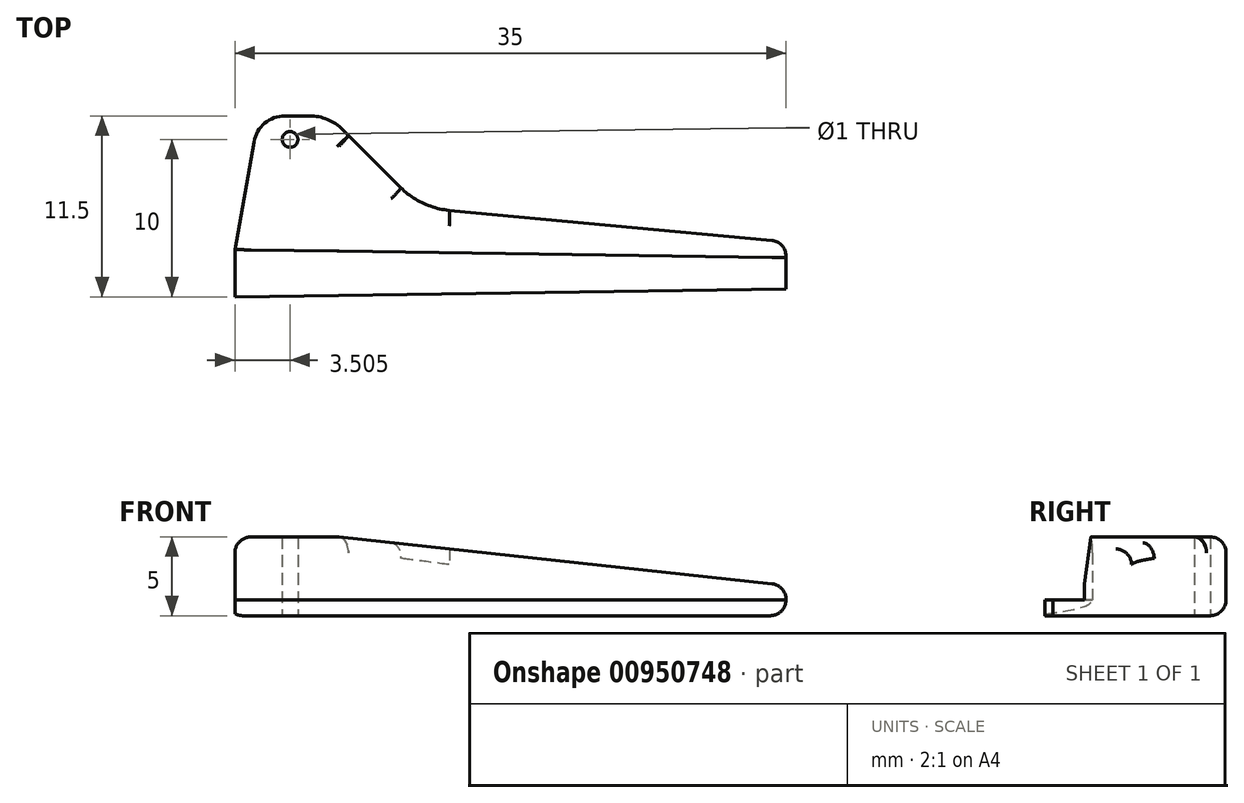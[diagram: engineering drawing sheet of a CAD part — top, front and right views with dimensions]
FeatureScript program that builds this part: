
annotation { "Feature Type Name" : "Feature", "Feature Type Description" : "" }
export const myFeature = defineFeature(function(context is Context, id is Id, definition is map)
    precondition{}
    {
        {
            var Q0;
            Q0=qCreatedBy(makeId("Top.planeOp"),FACE);
            var sketch = newSketch(context, id + "F0", { "sketchPlane" : qUnion([Q0])});
            skLineSegment(sketch, "E0", {"start": v(0.26, 1.5) * mm, "end": v(1.47, 8.35) * mm});
            skLineSegment(sketch, "E1", {"start": v(3.44, 10) * mm, "end": v(5, 10) * mm});
            skLineSegment(sketch, "E2", {"start": v(7.11, 9.12) * mm, "end": v(10.8, 5.44) * mm});
            skLineSegment(sketch, "E3", {"start": v(13.86, 4) * mm, "end": v(34.36, 2.08) * mm});
            skLineSegment(sketch, "E4", {"start": v(35.26, 1.09) * mm, "end": v(35.26, 0) * mm});
            skPoint(sketch, "E5.visualSharp", {"position": v(1.76, 10) * mm});
            skArc(sketch, "E5.filletArc", {"start": v(3.44, 10) * mm, "mid": v(2.16, 9.53) * mm, "end": v(1.47, 8.35) * mm});
            skPoint(sketch, "E6.visualSharp", {"position": v(6.23, 10) * mm});
            skArc(sketch, "E6.filletArc", {"start": v(7.11, 9.12) * mm, "mid": v(6.14, 9.77) * mm, "end": v(5, 10) * mm});
            skLineSegment(sketch, "E7", {"start": v(0.26, 1.5) * mm, "end": v(35.26, 1) * mm});
            skLineSegment(sketch, "E8", {"start": v(0.26, 1.5) * mm, "end": v(0.26, 0) * mm});
            skPoint(sketch, "E9.orphan", {"position": v(0, 0) * mm});
            skPoint(sketch, "E10.visualSharp", {"position": v(12.07, 4.17) * mm});
            skArc(sketch, "E10.filletArc", {"start": v(10.8, 5.44) * mm, "mid": v(12.2, 4.45) * mm, "end": v(13.86, 4) * mm});
            skLineSegment(sketch, "E11", {"start": v(1.23, 7) * mm, "end": v(9.23, 7) * mm, "construction": true});
            skCircle(sketch, "E12", {"center": v(3.76, 8.5) * mm, "radius": 0.5 * mm});
            skPoint(sketch, "E13.visualSharp", {"position": v(35.26, 2) * mm});
            skArc(sketch, "E13.filletArc", {"start": v(35.26, 1.09) * mm, "mid": v(35, 1.76) * mm, "end": v(34.36, 2.08) * mm});
            skArc(sketch, "E14.MirrorCS", {"start": v(35.26, -1.09) * mm, "mid": v(35, -1.76) * mm, "end": v(34.36, -2.08) * mm});
            skPoint(sketch, "E15.MirrorP", {"position": v(1.76, -10) * mm});
            skArc(sketch, "E16.MirrorCS", {"start": v(7.11, -9.12) * mm, "mid": v(6.14, -9.77) * mm, "end": v(5, -10) * mm});
            skArc(sketch, "E17.MirrorCS", {"start": v(10.8, -5.44) * mm, "mid": v(12.2, -4.45) * mm, "end": v(13.86, -4) * mm});
            skLineSegment(sketch, "E18.MirrorCS", {"start": v(3.44, -10) * mm, "end": v(5, -10) * mm});
            skPoint(sketch, "E19.MirrorP", {"position": v(35.26, -2) * mm});
            skCircle(sketch, "E20.MirrorC", {"center": v(3.76, -8.5) * mm, "radius": 0.5 * mm});
            skLineSegment(sketch, "E21.MirrorCS", {"start": v(7.11, -9.12) * mm, "end": v(10.8, -5.44) * mm});
            skLineSegment(sketch, "E22.MirrorCS", {"start": v(0.26, -1.5) * mm, "end": v(35.26, -1) * mm});
            skLineSegment(sketch, "E23.MirrorCS", {"start": v(1.23, -7) * mm, "end": v(9.23, -7) * mm, "construction": true});
            skPoint(sketch, "E24.MirrorP", {"position": v(6.23, -10) * mm});
            skArc(sketch, "E25.MirrorCS", {"start": v(3.44, -10) * mm, "mid": v(2.16, -9.53) * mm, "end": v(1.47, -8.35) * mm});
            skPoint(sketch, "E26.MirrorP", {"position": v(12.07, -4.17) * mm});
            skLineSegment(sketch, "E27.MirrorCS", {"start": v(0.26, -1.5) * mm, "end": v(1.47, -8.35) * mm});
            skLineSegment(sketch, "E28.MirrorCS", {"start": v(13.86, -4) * mm, "end": v(34.36, -2.08) * mm});
            skLineSegment(sketch, "E29.MirrorCS", {"start": v(0.26, -1.5) * mm, "end": v(0.26, 0) * mm});
            skLineSegment(sketch, "E30.MirrorCS", {"start": v(35.26, -1.09) * mm, "end": v(35.26, 0) * mm});
            skSolve(sketch);
        }
        {
            var Q0;
            Q0=makeQuery(id+"F0.imprint","IMPRINT",FACE,{"disambiguationData":[TD([[makeQuery(id+"F0.imprint","IMPRINT",EDGE,{"derivedFrom":sQuery(id+"F0.wireOp",EDGE,"E0")}),-1.0]])]});
            var Q1;
            {var subQ1=sQuery(id+"F0.wireOp",EDGE,"E7");Q1=makeQuery(id+"F0.imprint","IMPRINT",FACE,{"disambiguationData":[TD([[makeQuery(id+"F0.imprint","IMPRINT",EDGE,{"derivedFrom":subQ1}),-1.0]])]});}
            var Q2;
            {var subQ1=sQuery(id+"F0.wireOp",EDGE,"E14.MirrorCS");Q2=makeQuery(id+"F0.imprint","IMPRINT",FACE,{"disambiguationData":[TD([[makeQuery(id+"F0.imprint","IMPRINT",EDGE,{"derivedFrom":subQ1}),-1.0]])]});}
            extrude(context, id + "F1", {"entities" : qUnion([Q0, Q1, Q2]), "depth" : 1 * mm, "offsetDistance" : 25 * mm});
        }
        {
            var Q0;
            Q0=makeQuery(id+"F0.imprint","IMPRINT",FACE,{"disambiguationData":[TD([[makeQuery(id+"F0.imprint","IMPRINT",EDGE,{"derivedFrom":sQuery(id+"F0.wireOp",EDGE,"E0")}),-1.0]])]});
            var Q1;
            {var subQ1=sQuery(id+"F0.wireOp",EDGE,"E14.MirrorCS");Q1=makeQuery(id+"F0.imprint","IMPRINT",FACE,{"disambiguationData":[TD([[makeQuery(id+"F0.imprint","IMPRINT",EDGE,{"derivedFrom":subQ1}),-1.0]])]});}
            extrude(context, id + "F2", {"entities" : qUnion([Q0, Q1]), "operationType" : NewBodyOperationType.ADD, "depth" : 5 * mm, "offsetDistance" : 25 * mm});
        }
        {
            var Q0;
            Q0=qCreatedBy(makeId("Right.planeOp"),FACE);
            var sketch = newSketch(context, id + "F3", { "sketchPlane" : qUnion([Q0])});
            skCircle(sketch, "E31", {"center": v(-6.5, 2.5) * mm, "radius": 1.25 * mm});
            skCircle(sketch, "E32.MirrorC", {"center": v(6.5, 2.5) * mm, "radius": 1.25 * mm});
            skSolve(sketch);
        }
        {
            var Q0;
            Q0=makeQuery(id+"F3.imprint","IMPRINT",FACE,{"disambiguationData":[TD([[makeQuery(id+"F3.imprint","IMPRINT",EDGE,{"derivedFrom":sQuery(id+"F3.wireOp",EDGE,"E32.MirrorC")}),-1.0]])]});
            var Q1;
            Q1=makeQuery(id+"F3.imprint","IMPRINT",FACE,{"disambiguationData":[TD([[makeQuery(id+"F3.imprint","IMPRINT",EDGE,{"derivedFrom":sQuery(id+"F3.wireOp",EDGE,"E31")}),1.0]])]});
            extrude(context, id + "F4", {"entities" : qUnion([Q0, Q1]), "operationType" : NewBodyOperationType.REMOVE, "depth" : 25 * mm, "offsetDistance" : 25 * mm});
        }
        {
            var Q0;
            {var subQ0=sQuery(id+"F0.wireOp",EDGE,"E3");Q0=makeQuery(id+"F2.boolean.opBoolean","MERGE",FACE,{"derivedFrom":[makeQuery(id+"F1.opExtrude","SWEPT_FACE",FACE,{"disambiguationData":[OSD([subQ0])]}),makeQuery(id+"F2.opExtrude","SWEPT_FACE",FACE,{"disambiguationData":[OSD([subQ0])]})]});}
            var Q1;
            {var subQ0=sQuery(id+"F0.wireOp",EDGE,"E28.MirrorCS");Q1=makeQuery(id+"F2.boolean.opBoolean","MERGE",FACE,{"derivedFrom":[makeQuery(id+"F1.opExtrude","SWEPT_FACE",FACE,{"disambiguationData":[OSD([subQ0])]}),makeQuery(id+"F2.opExtrude","SWEPT_FACE",FACE,{"disambiguationData":[OSD([subQ0])]})]});}
            fillet(context, id + "F5", {"entities" : qUnion([Q0, Q1]), "radius" : 1 * mm, "tangentPropagation" : true, "allowEdgeOverflow" : false});
        }
        {
            var Q0;
            Q0=qCreatedBy(makeId("Front.planeOp"),FACE);
            var sketch = newSketch(context, id + "F6", { "sketchPlane" : qUnion([Q0])});
            skLineSegment(sketch, "E33", {"start": v(5.92, 5.1) * mm, "end": v(35.38, 1.92) * mm});
            skLineSegment(sketch, "E34", {"start": v(35.38, 1.92) * mm, "end": v(35.38, 7.22) * mm});
            skLineSegment(sketch, "E35", {"start": v(35.38, 7.22) * mm, "end": v(6.16, 7.22) * mm});
            skLineSegment(sketch, "E36", {"start": v(6.16, 7.22) * mm, "end": v(5.92, 5.1) * mm});
            skSolve(sketch);
        }
        {
            var Q0;
            Q0=makeQuery(id+"F6.imprint","IMPRINT",FACE,{"disambiguationData":[TD([[makeQuery(id+"F6.imprint","IMPRINT",EDGE,{"derivedFrom":sQuery(id+"F6.wireOp",EDGE,"E33")}),1.0]])]});
            extrude(context, id + "F7", {"entities" : qUnion([Q0]), "operationType" : NewBodyOperationType.REMOVE, "endBound" : BoundingType.SYMMETRIC, "depth" : 25 * mm, "offsetDistance" : 25 * mm});
        }
        {
            var Q0;
            {var subQ0=sQuery(id+"F0.wireOp",EDGE,"E3");Q0=makeQuery(id+"F7.boolean.opBoolean","INTERSECT",EDGE,{"derivedFrom":[makeQuery(id+"F2.boolean.opBoolean","MERGE",FACE,{"derivedFrom":[makeQuery(id+"F1.opExtrude","SWEPT_FACE",FACE,{"disambiguationData":[OSD([subQ0])]}),makeQuery(id+"F2.opExtrude","SWEPT_FACE",FACE,{"disambiguationData":[OSD([subQ0])]})]}),makeQuery(id+"F7.opExtrude","SWEPT_FACE",FACE,{"disambiguationData":[OSD([sQuery(id+"F6.wireOp",EDGE,"E33")])]})]});}
            var Q1;
            {var subQ0=sQuery(id+"F0.wireOp",EDGE,"E28.MirrorCS");Q1=makeQuery(id+"F7.boolean.opBoolean","INTERSECT",EDGE,{"derivedFrom":[makeQuery(id+"F2.boolean.opBoolean","MERGE",FACE,{"derivedFrom":[makeQuery(id+"F1.opExtrude","SWEPT_FACE",FACE,{"disambiguationData":[OSD([subQ0])]}),makeQuery(id+"F2.opExtrude","SWEPT_FACE",FACE,{"disambiguationData":[OSD([subQ0])]})]}),makeQuery(id+"F7.opExtrude","SWEPT_FACE",FACE,{"disambiguationData":[OSD([sQuery(id+"F6.wireOp",EDGE,"E33")])]})]});}
            fillet(context, id + "F8", {"entities" : qUnion([Q0, Q1]), "radius" : 1 * mm, "tangentPropagation" : true, "allowEdgeOverflow" : false});
        }
    });
